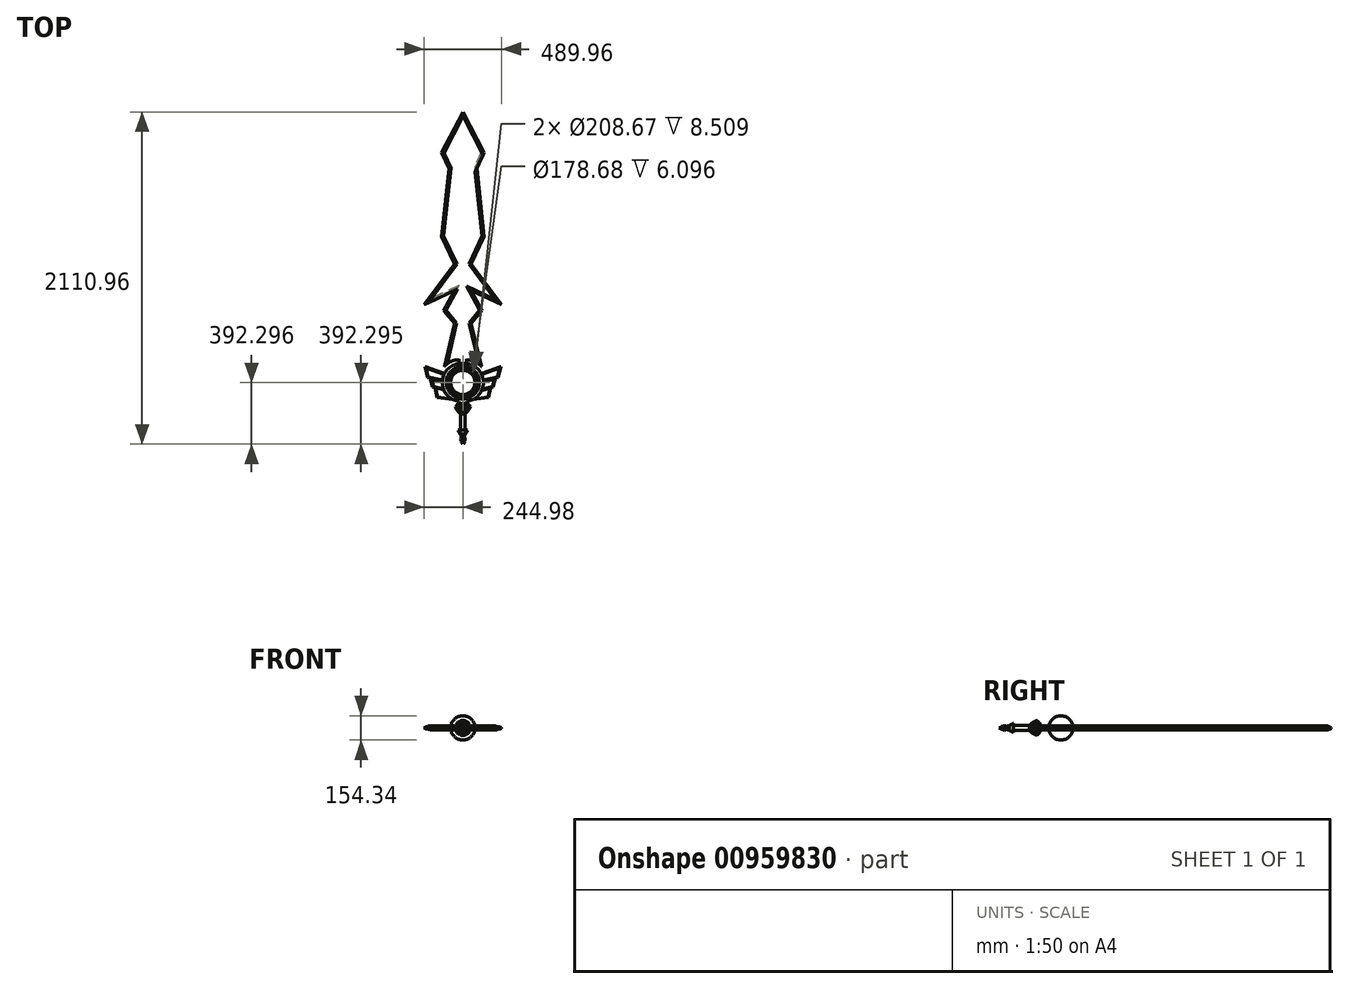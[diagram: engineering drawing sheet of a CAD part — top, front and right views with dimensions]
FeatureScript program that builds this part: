
annotation { "Feature Type Name" : "Feature", "Feature Type Description" : "" }
export const myFeature = defineFeature(function(context is Context, id is Id, definition is map)
    precondition{}
    {
        {
            var Q0;
            Q0=qCreatedBy(makeId("Top.planeOp"),FACE);
            var sketch = newSketch(context, id + "F0", { "sketchPlane" : qUnion([Q0])});
            skLineSegment(sketch, "E0", {"start": v(0, -149.6) * mm, "end": v(-9.38, -131.9) * mm});
            skLineSegment(sketch, "E1", {"start": v(-9.38, -131.9) * mm, "end": v(-14.6, -115.04) * mm});
            skLineSegment(sketch, "E2", {"start": v(-14.6, -115.04) * mm, "end": v(-9.38, -103.09) * mm});
            skLineSegment(sketch, "E3", {"start": v(-9.38, -103.09) * mm, "end": v(-14.6, -84.96) * mm});
            skLineSegment(sketch, "E4", {"start": v(-14.6, -84.96) * mm, "end": v(-29.25, -60.28) * mm});
            skLineSegment(sketch, "E5", {"start": v(-14.63, -60.28) * mm, "end": v(-14.63, 41.32) * mm});
            skLineSegment(sketch, "E6", {"start": v(-14.63, 41.32) * mm, "end": v(-31.03, 57.56) * mm});
            skLineSegment(sketch, "E7", {"start": v(-31.03, 57.56) * mm, "end": v(-39.11, 70.4) * mm});
            skLineSegment(sketch, "E8", {"start": v(-39.11, 70.4) * mm, "end": v(-47.67, 89.62) * mm});
            skLineSegment(sketch, "E9", {"start": v(0, 89.62) * mm, "end": v(0, -149.6) * mm});
            skLineSegment(sketch, "E10", {"start": v(-29.25, -60.28) * mm, "end": v(-14.63, -60.28) * mm});
            skLineSegment(sketch, "E11", {"start": v(-47.67, 89.62) * mm, "end": v(-29.25, 110.3) * mm});
            skLineSegment(sketch, "E12", {"start": v(-29.25, 110.3) * mm, "end": v(0, 110.3) * mm});
            skLineSegment(sketch, "E13", {"start": v(0, 110.3) * mm, "end": v(0, 89.62) * mm});
            skLineSegment(sketch, "E14", {"start": v(-23.2, 110.3) * mm, "end": v(-23.2, 122.53) * mm});
            skArc(sketch, "E15", {"start": v(-23.2, 362.86) * mm, "mid": v(-130.95, 242.7) * mm, "end": v(-23.2, 122.53) * mm});
            skLineSegment(sketch, "E16", {"start": v(-23.2, 362.86) * mm, "end": v(-23.2, 386.13) * mm});
            skLineSegment(sketch, "E17.MirrorCS", {"start": v(29.25, 110.3) * mm, "end": v(0, 110.3) * mm});
            skLineSegment(sketch, "E18.MirrorCS", {"start": v(23.2, 110.3) * mm, "end": v(23.2, 122.53) * mm});
            skArc(sketch, "E19.MirrorCS", {"start": v(23.2, 362.86) * mm, "mid": v(130.95, 242.7) * mm, "end": v(23.2, 122.53) * mm});
            skLineSegment(sketch, "E20.MirrorCS", {"start": v(23.2, 362.86) * mm, "end": v(23.2, 386.13) * mm});
            skArc(sketch, "E21", {"start": v(-23.2, 386.13) * mm, "mid": v(-75.52, 375.9) * mm, "end": v(-117.55, 343.11) * mm});
            skCircle(sketch, "E22", {"center": v(0, 242.7) * mm, "radius": 104.33 * mm});
            skArc(sketch, "E23", {"start": v(0, 319.87) * mm, "mid": v(-77.17, 242.7) * mm, "end": v(0, 165.52) * mm});
            skLineSegment(sketch, "E24", {"start": v(0, 319.87) * mm, "end": v(0, 165.52) * mm});
            skLineSegment(sketch, "E25", {"start": v(-117.55, 343.11) * mm, "end": v(-53.2, 615.72) * mm});
            skLineSegment(sketch, "E26.MirrorCS", {"start": v(117.55, 343.11) * mm, "end": v(53.2, 615.72) * mm});
            skArc(sketch, "E27.MirrorCS", {"start": v(23.2, 386.13) * mm, "mid": v(75.52, 375.9) * mm, "end": v(117.55, 343.11) * mm});
            skLineSegment(sketch, "E28", {"start": v(-53.2, 615.72) * mm, "end": v(-121.5, 700.46) * mm});
            skLineSegment(sketch, "E29", {"start": v(-121.5, 700.46) * mm, "end": v(-53.2, 826.55) * mm});
            skLineSegment(sketch, "E30", {"start": v(0, 1961.36) * mm, "end": v(-134.49, 1701.3) * mm});
            skLineSegment(sketch, "E31", {"start": v(-134.49, 1701.3) * mm, "end": v(-88.72, 1601.18) * mm});
            skLineSegment(sketch, "E32", {"start": v(-88.72, 1601.18) * mm, "end": v(-134.49, 1169.24) * mm});
            skLineSegment(sketch, "E33", {"start": v(-134.49, 1169.24) * mm, "end": v(-53.2, 995) * mm});
            skLineSegment(sketch, "E34.MirrorCS", {"start": v(53.2, 615.72) * mm, "end": v(121.5, 700.46) * mm});
            skLineSegment(sketch, "E35.MirrorCS", {"start": v(134.49, 1701.3) * mm, "end": v(88.72, 1601.18) * mm});
            skLineSegment(sketch, "E36.MirrorCS", {"start": v(88.72, 1601.18) * mm, "end": v(134.49, 1169.24) * mm});
            skLineSegment(sketch, "E37.MirrorCS", {"start": v(121.5, 700.46) * mm, "end": v(53.2, 826.55) * mm});
            skLineSegment(sketch, "E38.MirrorCS", {"start": v(134.49, 1169.24) * mm, "end": v(53.2, 995) * mm});
            skLineSegment(sketch, "E39.MirrorCS", {"start": v(0, 1961.36) * mm, "end": v(134.49, 1701.3) * mm});
            skLineSegment(sketch, "E40", {"start": v(-117.07, 298.93) * mm, "end": v(-240.89, 342.5) * mm});
            skLineSegment(sketch, "E41", {"start": v(-240.89, 342.5) * mm, "end": v(-224.82, 274.23) * mm});
            skLineSegment(sketch, "E42", {"start": v(-224.82, 274.23) * mm, "end": v(-130.6, 251.99) * mm});
            skLineSegment(sketch, "E43", {"start": v(-207.26, 270.09) * mm, "end": v(-191.7, 212.99) * mm});
            skLineSegment(sketch, "E44", {"start": v(-191.7, 212.99) * mm, "end": v(-121.77, 196.48) * mm});
            skLineSegment(sketch, "E45", {"start": v(-177.65, 209.67) * mm, "end": v(-164.52, 145.7) * mm});
            skLineSegment(sketch, "E46", {"start": v(-164.52, 145.7) * mm, "end": v(-57.59, 131.55) * mm});
            skLineSegment(sketch, "E47.MirrorCS", {"start": v(117.07, 298.93) * mm, "end": v(240.89, 342.5) * mm});
            skLineSegment(sketch, "E48.MirrorCS", {"start": v(224.82, 274.23) * mm, "end": v(130.6, 251.99) * mm});
            skLineSegment(sketch, "E49.MirrorCS", {"start": v(191.7, 212.99) * mm, "end": v(121.77, 196.48) * mm});
            skLineSegment(sketch, "E50.MirrorCS", {"start": v(164.52, 145.7) * mm, "end": v(57.59, 131.55) * mm});
            skLineSegment(sketch, "E51.MirrorCS", {"start": v(207.26, 270.09) * mm, "end": v(191.7, 212.99) * mm});
            skLineSegment(sketch, "E52.MirrorCS", {"start": v(177.65, 209.67) * mm, "end": v(164.52, 145.7) * mm});
            skLineSegment(sketch, "E53.MirrorCS", {"start": v(240.89, 342.5) * mm, "end": v(224.82, 274.23) * mm});
            skLineSegment(sketch, "E54", {"start": v(-53.2, 826.55) * mm, "end": v(-244.98, 737.08) * mm});
            skLineSegment(sketch, "E55", {"start": v(-244.98, 737.08) * mm, "end": v(-53.2, 995) * mm});
            skLineSegment(sketch, "E56.MirrorCS", {"start": v(244.98, 737.08) * mm, "end": v(53.2, 995) * mm});
            skLineSegment(sketch, "E57.MirrorCS", {"start": v(53.2, 826.55) * mm, "end": v(244.98, 737.08) * mm});
            skLineSegment(sketch, "E58", {"start": v(-23.2, 362.86) * mm, "end": v(23.2, 362.86) * mm});
            skSolve(sketch);
        }
        {
            var Q0;
            Q0=makeQuery(id+"F0.imprint","IMPRINT",FACE,{"disambiguationData":[TD([[makeQuery(id+"F0.imprint","IMPRINT",EDGE,{"derivedFrom":sQuery(id+"F0.wireOp",EDGE,"E23")}),1.0]])]});
            var Q1;
            Q1=sQuery(id+"F0.wireOp",EDGE,"E24");
            revolve(context, id + "F1", {"surfaceOperationType" : NewSurfaceOperationType.NEW, "entities" : qUnion([Q0]), "axis" : qUnion([Q1]), "revolveType" : RevolveType.FULL});
        }
        {
            var Q0;
            Q0=makeQuery(id+"F0.imprint","IMPRINT",FACE,{"disambiguationData":[TD([[makeQuery(id+"F0.imprint","IMPRINT",EDGE,{"derivedFrom":sQuery(id+"F0.wireOp",EDGE,"E0")}),-1.0]])]});
            var Q1;
            Q1=sQuery(id+"F0.wireOp",EDGE,"E9");
            revolve(context, id + "F2", {"surfaceOperationType" : NewSurfaceOperationType.NEW, "entities" : qUnion([Q0]), "axis" : qUnion([Q1]), "revolveType" : RevolveType.FULL});
        }
        {
            var Q0;
            {var subQ1=sQuery(id+"F0.wireOp",EDGE,"E40");Q0=makeQuery(id+"F0.imprint","IMPRINT",FACE,{"disambiguationData":[TD([[makeQuery(id+"F0.imprint","IMPRINT",EDGE,{"derivedFrom":subQ1}),1.0]])]});}
            var Q1;
            {var subQ0=sQuery(id+"F0.wireOp",EDGE,"E53.MirrorCS");Q1=makeQuery(id+"F0.imprint","IMPRINT",FACE,{"disambiguationData":[TD([[makeQuery(id+"F0.imprint","IMPRINT",EDGE,{"derivedFrom":subQ0}),-1.0]])]});}
            extrude(context, id + "F3", {"entities" : qUnion([Q0, Q1]), "endBound" : BoundingType.SYMMETRIC, "depth" : 14.48 * mm, "offsetDistance" : 25.4 * mm});
        }
        {
            var Q0;
            {var subQ5=sQuery(id+"F0.wireOp",EDGE,"E14");Q0=makeQuery(id+"F0.imprint","IMPRINT",FACE,{"disambiguationData":[TD([[makeQuery(id+"F0.imprint","IMPRINT",EDGE,{"derivedFrom":subQ5}),-1.0]])]});}
            extrude(context, id + "F4", {"entities" : qUnion([Q0]), "endBound" : BoundingType.SYMMETRIC, "depth" : 23.1 * mm, "offsetDistance" : 25.4 * mm});
        }
        {
            var Q0;
            {var subQ6=sQuery(id+"F0.wireOp",EDGE,"E51.MirrorCS");Q0=makeQuery(id+"F0.imprint","IMPRINT",FACE,{"disambiguationData":[TD([[makeQuery(id+"F0.imprint","IMPRINT",EDGE,{"derivedFrom":subQ6}),-1.0]])]});}
            var Q1;
            {var subQ1=sQuery(id+"F0.wireOp",EDGE,"E43");Q1=makeQuery(id+"F0.imprint","IMPRINT",FACE,{"disambiguationData":[TD([[makeQuery(id+"F0.imprint","IMPRINT",EDGE,{"derivedFrom":subQ1}),1.0]])]});}
            extrude(context, id + "F5", {"entities" : qUnion([Q0, Q1]), "endBound" : BoundingType.SYMMETRIC, "depth" : 10.67 * mm, "offsetDistance" : 25.4 * mm});
        }
        {
            var Q0;
            {var subQ4=sQuery(id+"F0.wireOp",EDGE,"E45");Q0=makeQuery(id+"F0.imprint","IMPRINT",FACE,{"disambiguationData":[TD([[makeQuery(id+"F0.imprint","IMPRINT",EDGE,{"derivedFrom":subQ4}),1.0]])]});}
            var Q1;
            {var subQ3=sQuery(id+"F0.wireOp",EDGE,"E50.MirrorCS");Q1=makeQuery(id+"F0.imprint","IMPRINT",FACE,{"disambiguationData":[TD([[makeQuery(id+"F0.imprint","IMPRINT",EDGE,{"derivedFrom":subQ3}),-1.0]])]});}
            extrude(context, id + "F6", {"entities" : qUnion([Q0, Q1]), "endBound" : BoundingType.SYMMETRIC, "oppositeDirection" : true, "depth" : 7.62 * mm, "offsetDistance" : 25.4 * mm});
        }
        {
            var Q0;
            Q0=makeQuery(id+"F0.imprint","IMPRINT",FACE,{"disambiguationData":[TD([[makeQuery(id+"F0.imprint","IMPRINT",EDGE,{"derivedFrom":sQuery(id+"F0.wireOp",EDGE,"E16")}),-1.0]])]});
            extrude(context, id + "F7", {"entities" : qUnion([Q0]), "operationType" : NewBodyOperationType.ADD, "endBound" : BoundingType.SYMMETRIC, "depth" : 25.4 * mm, "offsetDistance" : 25.4 * mm});
        }
        {
            var Q0;
            Q0=makeQuery(id+"F0.imprint","IMPRINT",FACE,{"disambiguationData":[TD([[makeQuery(id+"F0.imprint","IMPRINT",EDGE,{"derivedFrom":sQuery(id+"F0.wireOp",EDGE,"E22")}),1.0]])]});
            var sketch = newSketch(context, id + "F8", { "sketchPlane" : qUnion([Q0])});
            skCircle(sketch, "E59", {"center": v(0, 242.7) * mm, "radius": 89.34 * mm});
            skSolve(sketch);
        }
        {
            var Q0;
            Q0=makeQuery(id+"F8.imprint","IMPRINT",FACE,{"disambiguationData":[TD([[makeQuery(id+"F8.imprint","IMPRINT",EDGE,{"derivedFrom":sQuery(id+"F8.wireOp",EDGE,"E59")}),-1.0]])]});
            extrude(context, id + "F9", {"entities" : qUnion([Q0]), "operationType" : NewBodyOperationType.ADD, "endBound" : BoundingType.SYMMETRIC, "oppositeDirection" : true, "depth" : 6.1 * mm, "offsetDistance" : 25.4 * mm});
        }
        {
            var Q0;
            Q0=makeQuery(id+"F7.opExtrude","CAP_EDGE",EDGE,{"disambiguationData":[OSD([sQuery(id+"F0.wireOp",EDGE,"E39.MirrorCS")])],"isStart":false});
            var Q1;
            Q1=makeQuery(id+"F7.opExtrude","CAP_EDGE",EDGE,{"disambiguationData":[OSD([sQuery(id+"F0.wireOp",EDGE,"E30")])],"isStart":false});
            var Q2;
            Q2=makeQuery(id+"F7.opExtrude","CAP_EDGE",EDGE,{"disambiguationData":[OSD([sQuery(id+"F0.wireOp",EDGE,"E35.MirrorCS")])],"isStart":true});
            var Q3;
            Q3=makeQuery(id+"F7.opExtrude","CAP_EDGE",EDGE,{"disambiguationData":[OSD([sQuery(id+"F0.wireOp",EDGE,"E31")])],"isStart":false});
            var Q4;
            Q4=makeQuery(id+"F7.opExtrude","CAP_EDGE",EDGE,{"disambiguationData":[OSD([sQuery(id+"F0.wireOp",EDGE,"E32")])],"isStart":false});
            var Q5;
            Q5=makeQuery(id+"F7.opExtrude","CAP_EDGE",EDGE,{"disambiguationData":[OSD([sQuery(id+"F0.wireOp",EDGE,"E36.MirrorCS")])],"isStart":false});
            var Q6;
            Q6=makeQuery(id+"F7.opExtrude","CAP_EDGE",EDGE,{"disambiguationData":[OSD([sQuery(id+"F0.wireOp",EDGE,"E33")])],"isStart":false});
            var Q7;
            Q7=makeQuery(id+"F7.opExtrude","CAP_EDGE",EDGE,{"disambiguationData":[OSD([sQuery(id+"F0.wireOp",EDGE,"E38.MirrorCS")])],"isStart":false});
            var Q8;
            Q8=makeQuery(id+"F7.opExtrude","CAP_EDGE",EDGE,{"disambiguationData":[OSD([sQuery(id+"F0.wireOp",EDGE,"E55")])],"isStart":false});
            var Q9;
            Q9=makeQuery(id+"F7.opExtrude","CAP_EDGE",EDGE,{"disambiguationData":[OSD([sQuery(id+"F0.wireOp",EDGE,"E56.MirrorCS")])],"isStart":false});
            var Q10;
            Q10=makeQuery(id+"F7.opExtrude","CAP_EDGE",EDGE,{"disambiguationData":[OSD([sQuery(id+"F0.wireOp",EDGE,"E57.MirrorCS")])],"isStart":false});
            var Q11;
            Q11=makeQuery(id+"F7.opExtrude","CAP_EDGE",EDGE,{"disambiguationData":[OSD([sQuery(id+"F0.wireOp",EDGE,"E54")])],"isStart":true});
            var Q12;
            Q12=makeQuery(id+"F7.opExtrude","CAP_EDGE",EDGE,{"disambiguationData":[OSD([sQuery(id+"F0.wireOp",EDGE,"E29")])],"isStart":false});
            var Q13;
            Q13=makeQuery(id+"F7.opExtrude","CAP_EDGE",EDGE,{"disambiguationData":[OSD([sQuery(id+"F0.wireOp",EDGE,"E37.MirrorCS")])],"isStart":false});
            var Q14;
            Q14=makeQuery(id+"F7.opExtrude","CAP_EDGE",EDGE,{"disambiguationData":[OSD([sQuery(id+"F0.wireOp",EDGE,"E28")])],"isStart":false});
            var Q15;
            Q15=makeQuery(id+"F7.opExtrude","CAP_EDGE",EDGE,{"disambiguationData":[OSD([sQuery(id+"F0.wireOp",EDGE,"E34.MirrorCS")])],"isStart":false});
            var Q16;
            Q16=makeQuery(id+"F7.opExtrude","CAP_EDGE",EDGE,{"disambiguationData":[OSD([sQuery(id+"F0.wireOp",EDGE,"E25")])],"isStart":false});
            var Q17;
            Q17=makeQuery(id+"F7.opExtrude","CAP_EDGE",EDGE,{"disambiguationData":[OSD([sQuery(id+"F0.wireOp",EDGE,"E26.MirrorCS")])],"isStart":false});
            chamfer(context, id + "F10", {"entities" : qUnion([Q0, Q1, Q2, Q3, Q4, Q5, Q6, Q7, Q8, Q9, Q10, Q11, Q12, Q13, Q14, Q15, Q16, Q17]), "width" : 12.7 * mm, "tangentPropagation" : true});
        }
        {
            var Q0;
            Q0=makeQuery(id+"F7.opExtrude","CAP_EDGE",EDGE,{"disambiguationData":[OSD([sQuery(id+"F0.wireOp",EDGE,"E25")])],"isStart":true});
            var Q1;
            Q1=makeQuery(id+"F7.opExtrude","CAP_EDGE",EDGE,{"disambiguationData":[OSD([sQuery(id+"F0.wireOp",EDGE,"E26.MirrorCS")])],"isStart":true});
            var Q2;
            Q2=makeQuery(id+"F7.opExtrude","CAP_EDGE",EDGE,{"disambiguationData":[OSD([sQuery(id+"F0.wireOp",EDGE,"E28")])],"isStart":true});
            var Q3;
            Q3=makeQuery(id+"F7.opExtrude","CAP_EDGE",EDGE,{"disambiguationData":[OSD([sQuery(id+"F0.wireOp",EDGE,"E34.MirrorCS")])],"isStart":true});
            var Q4;
            Q4=makeQuery(id+"F7.opExtrude","CAP_EDGE",EDGE,{"disambiguationData":[OSD([sQuery(id+"F0.wireOp",EDGE,"E29")])],"isStart":true});
            var Q5;
            Q5=makeQuery(id+"F7.opExtrude","CAP_EDGE",EDGE,{"disambiguationData":[OSD([sQuery(id+"F0.wireOp",EDGE,"E37.MirrorCS")])],"isStart":true});
            var Q6;
            {var subQ0=sQuery(id+"F0.wireOp",EDGE,"E54");Q6=makeQuery(id+"F10.opChamfer","BLEND_EDGE",EDGE,{"blendedFrom":[makeQuery(id+"F7.opExtrude","CAP_EDGE",EDGE,{"disambiguationData":[OSD([subQ0])],"isStart":true}),makeQuery(id+"F7.opExtrude","CAP_FACE",FACE,{"disambiguationData":[OSD([sQuery(id+"F0.wireOp",EDGE,"E16"),sQuery(id+"F0.wireOp",EDGE,"E20.MirrorCS"),sQuery(id+"F0.wireOp",EDGE,"E21"),sQuery(id+"F0.wireOp",EDGE,"E25"),sQuery(id+"F0.wireOp",EDGE,"E26.MirrorCS"),sQuery(id+"F0.wireOp",EDGE,"E27.MirrorCS"),sQuery(id+"F0.wireOp",EDGE,"E28"),sQuery(id+"F0.wireOp",EDGE,"E29"),sQuery(id+"F0.wireOp",EDGE,"E30"),sQuery(id+"F0.wireOp",EDGE,"E31"),sQuery(id+"F0.wireOp",EDGE,"E32"),sQuery(id+"F0.wireOp",EDGE,"E33"),sQuery(id+"F0.wireOp",EDGE,"E34.MirrorCS"),sQuery(id+"F0.wireOp",EDGE,"E35.MirrorCS"),sQuery(id+"F0.wireOp",EDGE,"E36.MirrorCS"),sQuery(id+"F0.wireOp",EDGE,"E37.MirrorCS"),sQuery(id+"F0.wireOp",EDGE,"E38.MirrorCS"),sQuery(id+"F0.wireOp",EDGE,"E39.MirrorCS"),subQ0,sQuery(id+"F0.wireOp",EDGE,"E55"),sQuery(id+"F0.wireOp",EDGE,"E56.MirrorCS"),sQuery(id+"F0.wireOp",EDGE,"E57.MirrorCS"),sQuery(id+"F0.wireOp",EDGE,"E58")])],"isStart":true})],"blendedInto":[makeQuery(id+"F7.opExtrude","CAP_FACE",FACE,{"disambiguationData":[OSD([sQuery(id+"F0.wireOp",EDGE,"E16"),sQuery(id+"F0.wireOp",EDGE,"E20.MirrorCS"),sQuery(id+"F0.wireOp",EDGE,"E21"),sQuery(id+"F0.wireOp",EDGE,"E25"),sQuery(id+"F0.wireOp",EDGE,"E26.MirrorCS"),sQuery(id+"F0.wireOp",EDGE,"E27.MirrorCS"),sQuery(id+"F0.wireOp",EDGE,"E28"),sQuery(id+"F0.wireOp",EDGE,"E29"),sQuery(id+"F0.wireOp",EDGE,"E30"),sQuery(id+"F0.wireOp",EDGE,"E31"),sQuery(id+"F0.wireOp",EDGE,"E32"),sQuery(id+"F0.wireOp",EDGE,"E33"),sQuery(id+"F0.wireOp",EDGE,"E34.MirrorCS"),sQuery(id+"F0.wireOp",EDGE,"E35.MirrorCS"),sQuery(id+"F0.wireOp",EDGE,"E36.MirrorCS"),sQuery(id+"F0.wireOp",EDGE,"E37.MirrorCS"),sQuery(id+"F0.wireOp",EDGE,"E38.MirrorCS"),sQuery(id+"F0.wireOp",EDGE,"E39.MirrorCS"),subQ0,sQuery(id+"F0.wireOp",EDGE,"E55"),sQuery(id+"F0.wireOp",EDGE,"E56.MirrorCS"),sQuery(id+"F0.wireOp",EDGE,"E57.MirrorCS"),sQuery(id+"F0.wireOp",EDGE,"E58")])],"isStart":true})]});}
            var Q7;
            Q7=makeQuery(id+"F7.opExtrude","CAP_EDGE",EDGE,{"disambiguationData":[OSD([sQuery(id+"F0.wireOp",EDGE,"E57.MirrorCS")])],"isStart":true});
            var Q8;
            Q8=makeQuery(id+"F7.opExtrude","CAP_EDGE",EDGE,{"disambiguationData":[OSD([sQuery(id+"F0.wireOp",EDGE,"E56.MirrorCS")])],"isStart":true});
            var Q9;
            Q9=makeQuery(id+"F7.opExtrude","CAP_EDGE",EDGE,{"disambiguationData":[OSD([sQuery(id+"F0.wireOp",EDGE,"E55")])],"isStart":true});
            var Q10;
            Q10=makeQuery(id+"F7.opExtrude","CAP_EDGE",EDGE,{"disambiguationData":[OSD([sQuery(id+"F0.wireOp",EDGE,"E33")])],"isStart":true});
            var Q11;
            Q11=makeQuery(id+"F7.opExtrude","CAP_EDGE",EDGE,{"disambiguationData":[OSD([sQuery(id+"F0.wireOp",EDGE,"E38.MirrorCS")])],"isStart":true});
            var Q12;
            Q12=makeQuery(id+"F7.opExtrude","CAP_EDGE",EDGE,{"disambiguationData":[OSD([sQuery(id+"F0.wireOp",EDGE,"E36.MirrorCS")])],"isStart":true});
            var Q13;
            Q13=makeQuery(id+"F7.opExtrude","CAP_EDGE",EDGE,{"disambiguationData":[OSD([sQuery(id+"F0.wireOp",EDGE,"E32")])],"isStart":true});
            var Q14;
            Q14=makeQuery(id+"F7.opExtrude","CAP_EDGE",EDGE,{"disambiguationData":[OSD([sQuery(id+"F0.wireOp",EDGE,"E31")])],"isStart":true});
            var Q15;
            {var subQ0=sQuery(id+"F0.wireOp",EDGE,"E35.MirrorCS");Q15=makeQuery(id+"F10.opChamfer","BLEND_EDGE",EDGE,{"blendedFrom":[makeQuery(id+"F7.opExtrude","CAP_EDGE",EDGE,{"disambiguationData":[OSD([subQ0])],"isStart":true}),makeQuery(id+"F7.opExtrude","CAP_FACE",FACE,{"disambiguationData":[OSD([sQuery(id+"F0.wireOp",EDGE,"E16"),sQuery(id+"F0.wireOp",EDGE,"E20.MirrorCS"),sQuery(id+"F0.wireOp",EDGE,"E21"),sQuery(id+"F0.wireOp",EDGE,"E25"),sQuery(id+"F0.wireOp",EDGE,"E26.MirrorCS"),sQuery(id+"F0.wireOp",EDGE,"E27.MirrorCS"),sQuery(id+"F0.wireOp",EDGE,"E28"),sQuery(id+"F0.wireOp",EDGE,"E29"),sQuery(id+"F0.wireOp",EDGE,"E30"),sQuery(id+"F0.wireOp",EDGE,"E31"),sQuery(id+"F0.wireOp",EDGE,"E32"),sQuery(id+"F0.wireOp",EDGE,"E33"),sQuery(id+"F0.wireOp",EDGE,"E34.MirrorCS"),subQ0,sQuery(id+"F0.wireOp",EDGE,"E36.MirrorCS"),sQuery(id+"F0.wireOp",EDGE,"E37.MirrorCS"),sQuery(id+"F0.wireOp",EDGE,"E38.MirrorCS"),sQuery(id+"F0.wireOp",EDGE,"E39.MirrorCS"),sQuery(id+"F0.wireOp",EDGE,"E54"),sQuery(id+"F0.wireOp",EDGE,"E55"),sQuery(id+"F0.wireOp",EDGE,"E56.MirrorCS"),sQuery(id+"F0.wireOp",EDGE,"E57.MirrorCS"),sQuery(id+"F0.wireOp",EDGE,"E58")])],"isStart":true})],"blendedInto":[makeQuery(id+"F7.opExtrude","CAP_FACE",FACE,{"disambiguationData":[OSD([sQuery(id+"F0.wireOp",EDGE,"E16"),sQuery(id+"F0.wireOp",EDGE,"E20.MirrorCS"),sQuery(id+"F0.wireOp",EDGE,"E21"),sQuery(id+"F0.wireOp",EDGE,"E25"),sQuery(id+"F0.wireOp",EDGE,"E26.MirrorCS"),sQuery(id+"F0.wireOp",EDGE,"E27.MirrorCS"),sQuery(id+"F0.wireOp",EDGE,"E28"),sQuery(id+"F0.wireOp",EDGE,"E29"),sQuery(id+"F0.wireOp",EDGE,"E30"),sQuery(id+"F0.wireOp",EDGE,"E31"),sQuery(id+"F0.wireOp",EDGE,"E32"),sQuery(id+"F0.wireOp",EDGE,"E33"),sQuery(id+"F0.wireOp",EDGE,"E34.MirrorCS"),subQ0,sQuery(id+"F0.wireOp",EDGE,"E36.MirrorCS"),sQuery(id+"F0.wireOp",EDGE,"E37.MirrorCS"),sQuery(id+"F0.wireOp",EDGE,"E38.MirrorCS"),sQuery(id+"F0.wireOp",EDGE,"E39.MirrorCS"),sQuery(id+"F0.wireOp",EDGE,"E54"),sQuery(id+"F0.wireOp",EDGE,"E55"),sQuery(id+"F0.wireOp",EDGE,"E56.MirrorCS"),sQuery(id+"F0.wireOp",EDGE,"E57.MirrorCS"),sQuery(id+"F0.wireOp",EDGE,"E58")])],"isStart":true})]});}
            var Q16;
            Q16=makeQuery(id+"F7.opExtrude","CAP_EDGE",EDGE,{"disambiguationData":[OSD([sQuery(id+"F0.wireOp",EDGE,"E39.MirrorCS")])],"isStart":true});
            var Q17;
            Q17=makeQuery(id+"F7.opExtrude","CAP_EDGE",EDGE,{"disambiguationData":[OSD([sQuery(id+"F0.wireOp",EDGE,"E30")])],"isStart":true});
            chamfer(context, id + "F11", {"entities" : qUnion([Q0, Q1, Q2, Q3, Q4, Q5, Q6, Q7, Q8, Q9, Q10, Q11, Q12, Q13, Q14, Q15, Q16, Q17]), "width" : 10.16 * mm, "tangentPropagation" : true});
        }
        {
            var Q0;
            Q0=makeQuery(id+"F3.opExtrude","CAP_EDGE",EDGE,{"disambiguationData":[OSD([sQuery(id+"F0.wireOp",EDGE,"E41")])],"isStart":false});
            var Q1;
            Q1=makeQuery(id+"F5.opExtrude","CAP_EDGE",EDGE,{"disambiguationData":[OSD([sQuery(id+"F0.wireOp",EDGE,"E43")])],"isStart":false});
            var Q2;
            Q2=makeQuery(id+"F6.opExtrude","CAP_EDGE",EDGE,{"disambiguationData":[OSD([sQuery(id+"F0.wireOp",EDGE,"E45")])],"isStart":true});
            var Q3;
            Q3=makeQuery(id+"F5.opExtrude","CAP_EDGE",EDGE,{"disambiguationData":[OSD([sQuery(id+"F0.wireOp",EDGE,"E44")])],"isStart":false});
            var Q4;
            Q4=makeQuery(id+"F5.opExtrude","CAP_EDGE",EDGE,{"disambiguationData":[OSD([sQuery(id+"F0.wireOp",EDGE,"E42")])],"isStart":false});
            var Q5;
            Q5=makeQuery(id+"F3.opExtrude","CAP_EDGE",EDGE,{"disambiguationData":[OSD([sQuery(id+"F0.wireOp",EDGE,"E42")])],"isStart":false});
            var Q6;
            Q6=makeQuery(id+"F3.opExtrude","CAP_EDGE",EDGE,{"disambiguationData":[OSD([sQuery(id+"F0.wireOp",EDGE,"E40")])],"isStart":false});
            var Q7;
            Q7=makeQuery(id+"F6.opExtrude","CAP_EDGE",EDGE,{"disambiguationData":[OSD([sQuery(id+"F0.wireOp",EDGE,"E46")])],"isStart":true});
            var Q8;
            Q8=makeQuery(id+"F6.opExtrude","CAP_EDGE",EDGE,{"disambiguationData":[OSD([sQuery(id+"F0.wireOp",EDGE,"E50.MirrorCS")])],"isStart":true});
            var Q9;
            Q9=makeQuery(id+"F6.opExtrude","CAP_EDGE",EDGE,{"disambiguationData":[OSD([sQuery(id+"F0.wireOp",EDGE,"E52.MirrorCS")])],"isStart":true});
            var Q10;
            Q10=makeQuery(id+"F5.opExtrude","CAP_EDGE",EDGE,{"disambiguationData":[OSD([sQuery(id+"F0.wireOp",EDGE,"E51.MirrorCS")])],"isStart":false});
            var Q11;
            Q11=makeQuery(id+"F3.opExtrude","CAP_EDGE",EDGE,{"disambiguationData":[OSD([sQuery(id+"F0.wireOp",EDGE,"E53.MirrorCS")])],"isStart":false});
            var Q12;
            Q12=makeQuery(id+"F3.opExtrude","CAP_EDGE",EDGE,{"disambiguationData":[OSD([sQuery(id+"F0.wireOp",EDGE,"E47.MirrorCS")])],"isStart":false});
            var Q13;
            Q13=makeQuery(id+"F3.opExtrude","CAP_EDGE",EDGE,{"disambiguationData":[OSD([sQuery(id+"F0.wireOp",EDGE,"E48.MirrorCS")])],"isStart":false});
            var Q14;
            Q14=makeQuery(id+"F5.opExtrude","CAP_EDGE",EDGE,{"disambiguationData":[OSD([sQuery(id+"F0.wireOp",EDGE,"E49.MirrorCS")])],"isStart":false});
            var Q15;
            Q15=makeQuery(id+"F6.opExtrude","CAP_EDGE",EDGE,{"disambiguationData":[OSD([sQuery(id+"F0.wireOp",EDGE,"E49.MirrorCS")])],"isStart":true});
            var Q16;
            Q16=makeQuery(id+"F5.opExtrude","CAP_EDGE",EDGE,{"disambiguationData":[OSD([sQuery(id+"F0.wireOp",EDGE,"E48.MirrorCS")])],"isStart":false});
            chamfer(context, id + "F12", {"entities" : qUnion([Q0, Q1, Q2, Q3, Q4, Q5, Q6, Q7, Q8, Q9, Q10, Q11, Q12, Q13, Q14, Q15, Q16]), "width" : 5.08 * mm, "tangentPropagation" : true});
        }
        {
            var Q0;
            Q0=makeQuery(id+"F3.opExtrude","CAP_EDGE",EDGE,{"disambiguationData":[OSD([sQuery(id+"F0.wireOp",EDGE,"E41")])],"isStart":true});
            var Q1;
            Q1=makeQuery(id+"F5.opExtrude","CAP_EDGE",EDGE,{"disambiguationData":[OSD([sQuery(id+"F0.wireOp",EDGE,"E43")])],"isStart":true});
            var Q2;
            Q2=makeQuery(id+"F6.opExtrude","CAP_EDGE",EDGE,{"disambiguationData":[OSD([sQuery(id+"F0.wireOp",EDGE,"E45")])],"isStart":false});
            var Q3;
            Q3=makeQuery(id+"F3.opExtrude","CAP_EDGE",EDGE,{"disambiguationData":[OSD([sQuery(id+"F0.wireOp",EDGE,"E40")])],"isStart":true});
            var Q4;
            Q4=makeQuery(id+"F3.opExtrude","CAP_EDGE",EDGE,{"disambiguationData":[OSD([sQuery(id+"F0.wireOp",EDGE,"E42")])],"isStart":true});
            var Q5;
            Q5=makeQuery(id+"F5.opExtrude","CAP_EDGE",EDGE,{"disambiguationData":[OSD([sQuery(id+"F0.wireOp",EDGE,"E42")])],"isStart":true});
            var Q6;
            Q6=makeQuery(id+"F5.opExtrude","CAP_EDGE",EDGE,{"disambiguationData":[OSD([sQuery(id+"F0.wireOp",EDGE,"E44")])],"isStart":true});
            var Q7;
            Q7=makeQuery(id+"F6.opExtrude","CAP_EDGE",EDGE,{"disambiguationData":[OSD([sQuery(id+"F0.wireOp",EDGE,"E46")])],"isStart":false});
            var Q8;
            Q8=makeQuery(id+"F6.opExtrude","CAP_EDGE",EDGE,{"disambiguationData":[OSD([sQuery(id+"F0.wireOp",EDGE,"E50.MirrorCS")])],"isStart":false});
            var Q9;
            Q9=makeQuery(id+"F6.opExtrude","CAP_EDGE",EDGE,{"disambiguationData":[OSD([sQuery(id+"F0.wireOp",EDGE,"E52.MirrorCS")])],"isStart":false});
            var Q10;
            Q10=makeQuery(id+"F5.opExtrude","CAP_EDGE",EDGE,{"disambiguationData":[OSD([sQuery(id+"F0.wireOp",EDGE,"E49.MirrorCS")])],"isStart":true});
            var Q11;
            Q11=makeQuery(id+"F6.opExtrude","CAP_EDGE",EDGE,{"disambiguationData":[OSD([sQuery(id+"F0.wireOp",EDGE,"E49.MirrorCS")])],"isStart":false});
            var Q12;
            Q12=makeQuery(id+"F5.opExtrude","CAP_EDGE",EDGE,{"disambiguationData":[OSD([sQuery(id+"F0.wireOp",EDGE,"E51.MirrorCS")])],"isStart":true});
            var Q13;
            Q13=makeQuery(id+"F3.opExtrude","CAP_EDGE",EDGE,{"disambiguationData":[OSD([sQuery(id+"F0.wireOp",EDGE,"E48.MirrorCS")])],"isStart":true});
            var Q14;
            Q14=makeQuery(id+"F5.opExtrude","CAP_EDGE",EDGE,{"disambiguationData":[OSD([sQuery(id+"F0.wireOp",EDGE,"E48.MirrorCS")])],"isStart":true});
            var Q15;
            Q15=makeQuery(id+"F3.opExtrude","CAP_EDGE",EDGE,{"disambiguationData":[OSD([sQuery(id+"F0.wireOp",EDGE,"E53.MirrorCS")])],"isStart":true});
            var Q16;
            Q16=makeQuery(id+"F3.opExtrude","CAP_EDGE",EDGE,{"disambiguationData":[OSD([sQuery(id+"F0.wireOp",EDGE,"E47.MirrorCS")])],"isStart":true});
            chamfer(context, id + "F13", {"entities" : qUnion([Q0, Q1, Q2, Q3, Q4, Q5, Q6, Q7, Q8, Q9, Q10, Q11, Q12, Q13, Q14, Q15, Q16]), "width" : 5.08 * mm, "tangentPropagation" : true});
        }
        {
            var Q0;
            Q0=makeQuery(id+"F7.opExtrude","CAP_EDGE",EDGE,{"disambiguationData":[OSD([sQuery(id+"F0.wireOp",EDGE,"E27.MirrorCS")])],"isStart":true});
            var Q1;
            Q1=makeQuery(id+"F7.opExtrude","CAP_EDGE",EDGE,{"disambiguationData":[OSD([sQuery(id+"F0.wireOp",EDGE,"E21")])],"isStart":true});
            var Q2;
            Q2=makeQuery(id+"F7.opExtrude","CAP_EDGE",EDGE,{"disambiguationData":[OSD([sQuery(id+"F0.wireOp",EDGE,"E21")])],"isStart":false});
            var Q3;
            Q3=makeQuery(id+"F7.opExtrude","CAP_EDGE",EDGE,{"disambiguationData":[OSD([sQuery(id+"F0.wireOp",EDGE,"E27.MirrorCS")])],"isStart":false});
            fillet(context, id + "F14", {"entities" : qUnion([Q0, Q1, Q2, Q3]), "radius" : 5.08 * mm, "tangentPropagation" : true, "allowEdgeOverflow" : false});
        }
    });
